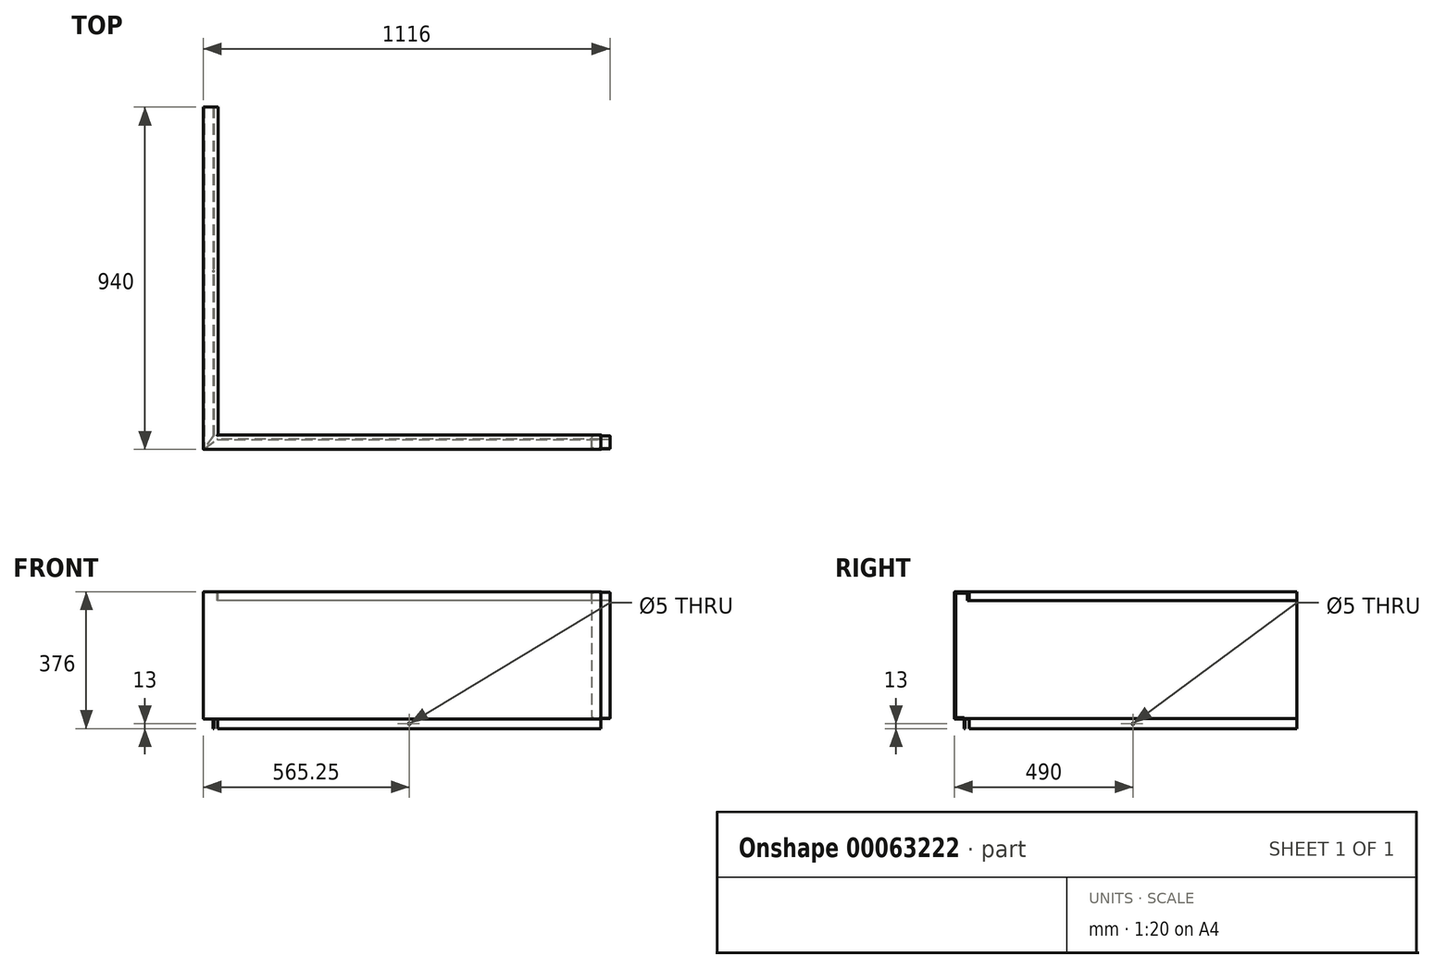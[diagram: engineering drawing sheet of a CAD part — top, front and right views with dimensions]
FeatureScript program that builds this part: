
annotation { "Feature Type Name" : "Feature", "Feature Type Description" : "" }
export const myFeature = defineFeature(function(context is Context, id is Id, definition is map)
    precondition{}
    {
        {
            var Q0;
            Q0=qCreatedBy(makeId("Right.planeOp"),FACE);
            var sketch = newSketch(context, id + "F0", { "sketchPlane" : qUnion([Q0])});
            skLineSegment(sketch, "E0.0", {"start": v(-40, -350) * mm, "end": v(-13, -350) * mm});
            skLineSegment(sketch, "E0.1", {"start": v(-40, 0) * mm, "end": v(-40, -350) * mm});
            skLineSegment(sketch, "E1", {"start": v(-38, -348) * mm, "end": v(-11, -348) * mm});
            skLineSegment(sketch, "E2", {"start": v(-38, -2) * mm, "end": v(-38, -348) * mm});
            skLineSegment(sketch, "E3", {"start": v(-2, -2) * mm, "end": v(-38, -2) * mm});
            skLineSegment(sketch, "E4", {"start": v(-2, -25) * mm, "end": v(-2, -2) * mm});
            skLineSegment(sketch, "E5", {"start": v(-13, -350) * mm, "end": v(-13, -376) * mm});
            skLineSegment(sketch, "E6", {"start": v(-11, -348) * mm, "end": v(-11, -376) * mm});
            skLineSegment(sketch, "E0.2", {"start": v(0, 0) * mm, "end": v(-40, 0) * mm});
            skLineSegment(sketch, "E0.3", {"start": v(0, -25) * mm, "end": v(0, 0) * mm});
            skLineSegment(sketch, "E7", {"start": v(0, -25) * mm, "end": v(-2, -25) * mm});
            skLineSegment(sketch, "E8", {"start": v(-11, -376) * mm, "end": v(-13, -376) * mm});
            skSolve(sketch);
        }
        {
            var Q0;
            Q0=makeQuery(id+"F0.imprint","IMPRINT",FACE,{"disambiguationData":[TD([[makeQuery(id+"F0.imprint","IMPRINT",EDGE,{"derivedFrom":sQuery(id+"F0.wireOp",EDGE,"E0.0")}),1.0]])]});
            extrude(context, id + "F1", {"entities" : qUnion([Q0]), "depth" : 1051 * mm, "hasSecondDirection" : true, "secondDirectionOppositeDirection" : true, "secondDirectionDepth" : .5 * mm});
        }
        {
            var Q0;
            Q0=qCreatedBy(makeId("Front.planeOp"),FACE);
            var sketch = newSketch(context, id + "F2", { "sketchPlane" : qUnion([Q0])});
            skLineSegment(sketch, "E9.0", {"start": v(-40, -350) * mm, "end": v(-13, -350) * mm});
            skLineSegment(sketch, "E9.1", {"start": v(-40, 0) * mm, "end": v(-40, -350) * mm});
            skLineSegment(sketch, "E10", {"start": v(-38, -348) * mm, "end": v(-11, -348) * mm});
            skLineSegment(sketch, "E11", {"start": v(-38, -2) * mm, "end": v(-38, -348) * mm});
            skLineSegment(sketch, "E12", {"start": v(-2, -2) * mm, "end": v(-38, -2) * mm});
            skLineSegment(sketch, "E13", {"start": v(-2, -25) * mm, "end": v(-2, -2) * mm});
            skLineSegment(sketch, "E14", {"start": v(-13, -350) * mm, "end": v(-13, -376) * mm});
            skLineSegment(sketch, "E15", {"start": v(-11, -348) * mm, "end": v(-11, -376) * mm});
            skLineSegment(sketch, "E9.2", {"start": v(0, 0) * mm, "end": v(-40, 0) * mm});
            skLineSegment(sketch, "E9.3", {"start": v(0, -25) * mm, "end": v(0, 0) * mm});
            skLineSegment(sketch, "E16", {"start": v(0, -25) * mm, "end": v(-2, -25) * mm});
            skLineSegment(sketch, "E17", {"start": v(-11, -376) * mm, "end": v(-13, -376) * mm});
            skSolve(sketch);
        }
        {
            var Q0;
            Q0=qSketchRegion(id+"F2",true);
            extrude(context, id + "F3", {"entities" : qUnion([Q0]), "oppositeDirection" : true, "depth" : 900 * mm});
        }
        {
            var Q0;
            Q0=qCreatedBy(makeId("Top.planeOp"),FACE);
            var sketch = newSketch(context, id + "F4", { "sketchPlane" : qUnion([Q0])});
            skLineSegment(sketch, "E18.top", {"start": v(0, 0) * mm, "end": v(-40, 0) * mm});
            skLineSegment(sketch, "E19.top", {"start": v(0, -40) * mm, "end": v(-40, -40) * mm});
            skLineSegment(sketch, "E19.left", {"start": v(0, 0) * mm, "end": v(0, -40) * mm});
            skLineSegment(sketch, "E19.right", {"start": v(-40, 0) * mm, "end": v(-40, -40) * mm});
            skSolve(sketch);
        }
        {
            var Q0;
            Q0=qSketchRegion(id+"F4",true);
            extrude(context, id + "F5", {"entities" : qUnion([Q0]), "oppositeDirection" : true, "depth" : 2 * mm});
        }
        {
            var Q0;
            Q0=makeQuery(id+"F5.opExtrude","CAP_FACE",FACE,{"disambiguationData":[OSD([sQuery(id+"F4.wireOp",EDGE,"E18.top"),sQuery(id+"F4.wireOp",EDGE,"E19.top"),sQuery(id+"F4.wireOp",EDGE,"E19.left"),sQuery(id+"F4.wireOp",EDGE,"E19.right")])],"isStart":false});
            var sketch = newSketch(context, id + "F6", { "sketchPlane" : qUnion([Q0])});
            skLineSegment(sketch, "E20.0", {"start": v(-40, 0) * mm, "end": v(-40, 40) * mm});
            skLineSegment(sketch, "E21.0", {"start": v(0, 40) * mm, "end": v(-40, 40) * mm});
            skLineSegment(sketch, "E22.0", {"start": v(0, 38) * mm, "end": v(-38, 38) * mm});
            skLineSegment(sketch, "E22.1", {"start": v(-38, 0) * mm, "end": v(-38, 38) * mm});
            skLineSegment(sketch, "E23", {"start": v(-38, 0) * mm, "end": v(-40, 0) * mm});
            skLineSegment(sketch, "E24", {"start": v(0, 40) * mm, "end": v(0, 38) * mm});
            skSolve(sketch);
        }
        {
            var Q0;
            Q0=makeQuery(id+"F6.imprint","IMPRINT",FACE,{"disambiguationData":[TD([[makeQuery(id+"F6.imprint","IMPRINT",EDGE,{"derivedFrom":sQuery(id+"F6.wireOp",EDGE,"E20.0")}),-1.0]])]});
            extrude(context, id + "F7", {"entities" : qUnion([Q0]), "depth" : 346 * mm});
        }
        {
            var Q0;
            Q0=makeQuery(id+"F7.opExtrude","CAP_FACE",FACE,{"disambiguationData":[OSD([sQuery(id+"F6.wireOp",EDGE,"E20.0"),sQuery(id+"F6.wireOp",EDGE,"E21.0"),sQuery(id+"F6.wireOp",EDGE,"E22.0"),sQuery(id+"F6.wireOp",EDGE,"E22.1"),sQuery(id+"F6.wireOp",EDGE,"E23"),sQuery(id+"F6.wireOp",EDGE,"E24")])],"isStart":false});
            var sketch = newSketch(context, id + "F8", { "sketchPlane" : qUnion([Q0])});
            skLineSegment(sketch, "E25.0", {"start": v(-40, 0) * mm, "end": v(-40, 40) * mm});
            skLineSegment(sketch, "E26.0", {"start": v(0, 40) * mm, "end": v(-40, 40) * mm});
            skLineSegment(sketch, "E27", {"start": v(-40, 0) * mm, "end": v(-11, 0) * mm});
            skLineSegment(sketch, "E28", {"start": v(-11, 0) * mm, "end": v(-38, 38) * mm});
            skLineSegment(sketch, "E29", {"start": v(-38, 38) * mm, "end": v(-0.5, 11) * mm});
            skLineSegment(sketch, "E30", {"start": v(-0.5, 11) * mm, "end": v(0, 40) * mm});
            skSolve(sketch);
        }
        {
            var Q0;
            Q0=qSketchRegion(id+"F8",true);
            extrude(context, id + "F9", {"entities" : qUnion([Q0]), "depth" : 2 * mm});
        }
        {
            var Q0;
            Q0=makeQuery(id+"F3.opExtrude","SWEPT_BODY",BODY,{"disambiguationData":[OSD([sQuery(id+"F2.wireOp",EDGE,"E9.0"),sQuery(id+"F2.wireOp",EDGE,"E9.1"),sQuery(id+"F2.wireOp",EDGE,"E10"),sQuery(id+"F2.wireOp",EDGE,"E11"),sQuery(id+"F2.wireOp",EDGE,"E12"),sQuery(id+"F2.wireOp",EDGE,"E13"),sQuery(id+"F2.wireOp",EDGE,"E14"),sQuery(id+"F2.wireOp",EDGE,"E15"),sQuery(id+"F2.wireOp",EDGE,"E9.2"),sQuery(id+"F2.wireOp",EDGE,"E9.3"),sQuery(id+"F2.wireOp",EDGE,"E16"),sQuery(id+"F2.wireOp",EDGE,"E17")])]});
            var Q1;
            Q1=makeQuery(id+"F7.opExtrude","SWEPT_BODY",BODY,{"disambiguationData":[OSD([sQuery(id+"F6.wireOp",EDGE,"E20.0"),sQuery(id+"F6.wireOp",EDGE,"E21.0"),sQuery(id+"F6.wireOp",EDGE,"E22.0"),sQuery(id+"F6.wireOp",EDGE,"E22.1"),sQuery(id+"F6.wireOp",EDGE,"E23"),sQuery(id+"F6.wireOp",EDGE,"E24")])]});
            var Q2;
            Q2=makeQuery(id+"F9.opExtrude","SWEPT_BODY",BODY,{"disambiguationData":[OSD([sQuery(id+"F8.wireOp",EDGE,"E25.0"),sQuery(id+"F8.wireOp",EDGE,"E26.0"),sQuery(id+"F8.wireOp",EDGE,"E27"),sQuery(id+"F8.wireOp",EDGE,"E28"),sQuery(id+"F8.wireOp",EDGE,"E29"),sQuery(id+"F8.wireOp",EDGE,"E30")])]});
            var Q3;
            Q3=makeQuery(id+"F5.opExtrude","SWEPT_BODY",BODY,{"disambiguationData":[OSD([sQuery(id+"F4.wireOp",EDGE,"E18.top"),sQuery(id+"F4.wireOp",EDGE,"E19.top"),sQuery(id+"F4.wireOp",EDGE,"E19.left"),sQuery(id+"F4.wireOp",EDGE,"E19.right")])]});
            booleanBodies(context, id + "F10", {"operationType" : BooleanOperationType.UNION, "tools" : qUnion([Q0, Q1, Q2, Q3])});
        }
        {
            var Q0;
            Q0=makeQuery(id+"F3.opExtrude","SWEPT_BODY",BODY,{"disambiguationData":[OSD([sQuery(id+"F2.wireOp",EDGE,"E9.0"),sQuery(id+"F2.wireOp",EDGE,"E9.1"),sQuery(id+"F2.wireOp",EDGE,"E10"),sQuery(id+"F2.wireOp",EDGE,"E11"),sQuery(id+"F2.wireOp",EDGE,"E12"),sQuery(id+"F2.wireOp",EDGE,"E13"),sQuery(id+"F2.wireOp",EDGE,"E14"),sQuery(id+"F2.wireOp",EDGE,"E15"),sQuery(id+"F2.wireOp",EDGE,"E9.2"),sQuery(id+"F2.wireOp",EDGE,"E9.3"),sQuery(id+"F2.wireOp",EDGE,"E16"),sQuery(id+"F2.wireOp",EDGE,"E17")])]});
            var Q1;
            Q1=makeQuery(id+"F1.opExtrude","SWEPT_BODY",BODY,{"disambiguationData":[OSD([sQuery(id+"F0.wireOp",EDGE,"E0.0"),sQuery(id+"F0.wireOp",EDGE,"E0.1"),sQuery(id+"F0.wireOp",EDGE,"E1"),sQuery(id+"F0.wireOp",EDGE,"E2"),sQuery(id+"F0.wireOp",EDGE,"E3"),sQuery(id+"F0.wireOp",EDGE,"E4"),sQuery(id+"F0.wireOp",EDGE,"E5"),sQuery(id+"F0.wireOp",EDGE,"E6"),sQuery(id+"F0.wireOp",EDGE,"E0.2"),sQuery(id+"F0.wireOp",EDGE,"E0.3"),sQuery(id+"F0.wireOp",EDGE,"E7"),sQuery(id+"F0.wireOp",EDGE,"E8")])]});
            booleanBodies(context, id + "F11", {"operationType" : BooleanOperationType.UNION, "tools" : qUnion([Q0, Q1])});
        }
        {
            var Q0;
            Q0=makeQuery(id+"F1.opExtrude","SWEPT_FACE",FACE,{"disambiguationData":[OSD([sQuery(id+"F0.wireOp",EDGE,"E5")])]});
            var sketch = newSketch(context, id + "F12", { "sketchPlane" : qUnion([Q0])});
            skLineSegment(sketch, "E31", {"start": v(-0.5, -363) * mm, "end": v(1051, -363) * mm});
            skPoint(sketch, "E32", {"position": v(525.25, -363) * mm});
            skSolve(sketch);
        }
        {
            var Q0;
            Q0=makeQuery(id+"F3.opExtrude","SWEPT_FACE",FACE,{"disambiguationData":[OSD([sQuery(id+"F2.wireOp",EDGE,"E14")])]});
            var sketch = newSketch(context, id + "F13", { "sketchPlane" : qUnion([Q0])});
            skLineSegment(sketch, "E33", {"start": v(-900, -363) * mm, "end": v(0, -363) * mm});
            skPoint(sketch, "E34", {"position": v(-450, -363) * mm});
            skSolve(sketch);
        }
        {
            var Q0;
            Q0=sQuery(id+"F13.wireOp",VERTEX,"E34");
            var Q1;
            Q1=sQuery(id+"F12.wireOp",VERTEX,"E32");
            var Q2;
            Q2=makeQuery(id+"F3.opExtrude","SWEPT_BODY",BODY,{"disambiguationData":[OSD([sQuery(id+"F2.wireOp",EDGE,"E9.0"),sQuery(id+"F2.wireOp",EDGE,"E9.1"),sQuery(id+"F2.wireOp",EDGE,"E10"),sQuery(id+"F2.wireOp",EDGE,"E11"),sQuery(id+"F2.wireOp",EDGE,"E12"),sQuery(id+"F2.wireOp",EDGE,"E13"),sQuery(id+"F2.wireOp",EDGE,"E14"),sQuery(id+"F2.wireOp",EDGE,"E15"),sQuery(id+"F2.wireOp",EDGE,"E9.2"),sQuery(id+"F2.wireOp",EDGE,"E9.3"),sQuery(id+"F2.wireOp",EDGE,"E16"),sQuery(id+"F2.wireOp",EDGE,"E17")])]});
            hole(context, id + "F14", {"style" : HoleStyle.SIMPLE, "holeDiameter" : 5 * mm, "endStyle" : HoleEndStyle.THROUGH, "locations" : qUnion([Q0, Q1]), "scope" : qUnion([Q2])});
        }
        {
            var Q0;
            Q0=makeQuery(id+"F1.opExtrude","CAP_FACE",FACE,{"disambiguationData":[OSD([sQuery(id+"F0.wireOp",EDGE,"E0.0"),sQuery(id+"F0.wireOp",EDGE,"E0.1"),sQuery(id+"F0.wireOp",EDGE,"E1"),sQuery(id+"F0.wireOp",EDGE,"E2"),sQuery(id+"F0.wireOp",EDGE,"E3"),sQuery(id+"F0.wireOp",EDGE,"E4"),sQuery(id+"F0.wireOp",EDGE,"E5"),sQuery(id+"F0.wireOp",EDGE,"E6"),sQuery(id+"F0.wireOp",EDGE,"E0.2"),sQuery(id+"F0.wireOp",EDGE,"E0.3"),sQuery(id+"F0.wireOp",EDGE,"E7"),sQuery(id+"F0.wireOp",EDGE,"E8")])],"isStart":false});
            var sketch = newSketch(context, id + "F15", { "sketchPlane" : qUnion([Q0])});
            skLineSegment(sketch, "E35.0", {"start": v(-36, -346) * mm, "end": v(-13, -346) * mm});
            skLineSegment(sketch, "E35.1", {"start": v(-36, -4) * mm, "end": v(-36, -346) * mm});
            skLineSegment(sketch, "E35.2", {"start": v(-4, -4) * mm, "end": v(-36, -4) * mm});
            skLineSegment(sketch, "E35.3", {"start": v(-4, -25) * mm, "end": v(-4, -4) * mm});
            skLineSegment(sketch, "E36.0", {"start": v(-2, -25) * mm, "end": v(-2, -2) * mm});
            skLineSegment(sketch, "E37.0", {"start": v(-2, -2) * mm, "end": v(-38, -2) * mm});
            skLineSegment(sketch, "E38.0", {"start": v(-38, -2) * mm, "end": v(-38, -348) * mm});
            skLineSegment(sketch, "E39.0", {"start": v(-38, -348) * mm, "end": v(-13, -348) * mm});
            skLineSegment(sketch, "E40", {"start": v(-13, -346) * mm, "end": v(-13, -348) * mm});
            skLineSegment(sketch, "E41", {"start": v(-4, -25) * mm, "end": v(-2, -25) * mm});
            skSolve(sketch);
        }
        {
            var Q0;
            Q0=qSketchRegion(id+"F15",true);
            extrude(context, id + "F16", {"entities" : qUnion([Q0]), "operationType" : NewBodyOperationType.ADD, "depth" : 25 * mm, "hasSecondDirection" : true, "secondDirectionOppositeDirection" : true, "secondDirectionDepth" : 25 * mm});
        }
        {
            var Q0;
            Q0=makeQuery(id+"F1.opExtrude","SWEPT_EDGE",EDGE,{"disambiguationData":[OSD([sQuery(id+"F0.wireOp",EDGE,"E0.2"),sQuery(id+"F0.wireOp",EDGE,"E0.3")])]});
            var Q1;
            Q1=makeQuery(id+"F16.opExtrude","SWEPT_EDGE",EDGE,{"disambiguationData":[OSD([sQuery(id+"F15.wireOp",EDGE,"E36.0"),sQuery(id+"F15.wireOp",EDGE,"E37.0")])]});
            var Q2;
            Q2=makeQuery(id+"F11.opBoolean","MERGE",EDGE,{"derivedFrom":[makeQuery(id+"F1.opExtrude","SWEPT_EDGE",EDGE,{"disambiguationData":[OSD([sQuery(id+"F0.wireOp",EDGE,"E0.1"),sQuery(id+"F0.wireOp",EDGE,"E0.2")])]}),makeQuery(id+"F5.opExtrude","CAP_EDGE",EDGE,{"disambiguationData":[OSD([sQuery(id+"F4.wireOp",EDGE,"E19.top")])],"isStart":true})]});
            var Q3;
            Q3=makeQuery(id+"F16.opExtrude","SWEPT_EDGE",EDGE,{"disambiguationData":[OSD([sQuery(id+"F15.wireOp",EDGE,"E37.0"),sQuery(id+"F15.wireOp",EDGE,"E38.0")])]});
            var Q4;
            Q4=makeQuery(id+"F10.opBoolean","MERGE",EDGE,{"derivedFrom":[makeQuery(id+"F3.opExtrude","SWEPT_EDGE",EDGE,{"disambiguationData":[OSD([sQuery(id+"F2.wireOp",EDGE,"E9.1"),sQuery(id+"F2.wireOp",EDGE,"E9.2")])]}),makeQuery(id+"F5.opExtrude","CAP_EDGE",EDGE,{"disambiguationData":[OSD([sQuery(id+"F4.wireOp",EDGE,"E19.right")])],"isStart":true})]});
            var Q5;
            Q5=makeQuery(id+"F10.opBoolean","MERGE",EDGE,{"derivedFrom":[makeQuery(id+"F3.opExtrude","SWEPT_EDGE",EDGE,{"disambiguationData":[OSD([sQuery(id+"F2.wireOp",EDGE,"E9.2"),sQuery(id+"F2.wireOp",EDGE,"E9.3")])]}),makeQuery(id+"F5.opExtrude","CAP_EDGE",EDGE,{"disambiguationData":[OSD([sQuery(id+"F4.wireOp",EDGE,"E19.left")])],"isStart":true})]});
            var Q6;
            Q6=makeQuery(id+"F3.opExtrude","SWEPT_EDGE",EDGE,{"disambiguationData":[OSD([sQuery(id+"F2.wireOp",EDGE,"E10"),sQuery(id+"F2.wireOp",EDGE,"E15")])]});
            var Q7;
            Q7=makeQuery(id+"F10.opBoolean","MERGE",EDGE,{"derivedFrom":[makeQuery(id+"F3.opExtrude","SWEPT_EDGE",EDGE,{"disambiguationData":[OSD([sQuery(id+"F2.wireOp",EDGE,"E10"),sQuery(id+"F2.wireOp",EDGE,"E11")])]}),makeQuery(id+"F7.opExtrude","CAP_EDGE",EDGE,{"disambiguationData":[OSD([sQuery(id+"F6.wireOp",EDGE,"E22.1")])],"isStart":false})]});
            var Q8;
            {var subQ0=sQuery(id+"F6.wireOp",EDGE,"E22.0");var subQ10=makeQuery(id+"F7.opExtrude","CAP_EDGE",EDGE,{"disambiguationData":[OSD([subQ0])],"isStart":false});Q8=makeQuery(id+"F11.opBoolean","MERGE",EDGE,{"derivedFrom":[makeQuery(id+"F1.opExtrude","SWEPT_EDGE",EDGE,{"disambiguationData":[OSD([sQuery(id+"F0.wireOp",EDGE,"E1"),sQuery(id+"F0.wireOp",EDGE,"E2")])]}),makeQuery(id+"F10.opBoolean","SPLIT",EDGE,{"disambiguationData":[TD([makeQuery(id+"F3.opExtrude","SWEPT_FACE",FACE,{"disambiguationData":[OSD([sQuery(id+"F2.wireOp",EDGE,"E9.3")])]})])],"derivedFrom":subQ10}),makeQuery(id+"F10.opBoolean","SPLIT",EDGE,{"disambiguationData":[TD([makeQuery(id+"F3.opExtrude","SWEPT_FACE",FACE,{"disambiguationData":[OSD([sQuery(id+"F2.wireOp",EDGE,"E10")])]})])],"derivedFrom":subQ10})]});}
            var Q9;
            Q9=makeQuery(id+"F1.opExtrude","SWEPT_EDGE",EDGE,{"disambiguationData":[OSD([sQuery(id+"F0.wireOp",EDGE,"E1"),sQuery(id+"F0.wireOp",EDGE,"E6")])]});
            var Q10;
            Q10=makeQuery(id+"F16.opExtrude","SWEPT_EDGE",EDGE,{"disambiguationData":[OSD([sQuery(id+"F15.wireOp",EDGE,"E35.0"),sQuery(id+"F15.wireOp",EDGE,"E35.1")])]});
            var Q11;
            Q11=makeQuery(id+"F1.opExtrude","SWEPT_EDGE",EDGE,{"disambiguationData":[OSD([sQuery(id+"F0.wireOp",EDGE,"E0.0"),sQuery(id+"F0.wireOp",EDGE,"E5")])]});
            var Q12;
            Q12=makeQuery(id+"F11.opBoolean","MERGE",EDGE,{"derivedFrom":[makeQuery(id+"F1.opExtrude","SWEPT_EDGE",EDGE,{"disambiguationData":[OSD([sQuery(id+"F0.wireOp",EDGE,"E0.0"),sQuery(id+"F0.wireOp",EDGE,"E0.1")])]}),makeQuery(id+"F9.opExtrude","CAP_EDGE",EDGE,{"disambiguationData":[OSD([sQuery(id+"F8.wireOp",EDGE,"E26.0")])],"isStart":false})]});
            var Q13;
            Q13=makeQuery(id+"F16.opExtrude","SWEPT_EDGE",EDGE,{"disambiguationData":[OSD([sQuery(id+"F15.wireOp",EDGE,"E38.0"),sQuery(id+"F15.wireOp",EDGE,"E39.0")])]});
            var Q14;
            Q14=makeQuery(id+"F3.opExtrude","SWEPT_EDGE",EDGE,{"disambiguationData":[OSD([sQuery(id+"F2.wireOp",EDGE,"E9.0"),sQuery(id+"F2.wireOp",EDGE,"E14")])]});
            var Q15;
            Q15=makeQuery(id+"F10.opBoolean","MERGE",EDGE,{"derivedFrom":[makeQuery(id+"F3.opExtrude","SWEPT_EDGE",EDGE,{"disambiguationData":[OSD([sQuery(id+"F2.wireOp",EDGE,"E9.0"),sQuery(id+"F2.wireOp",EDGE,"E9.1")])]}),makeQuery(id+"F9.opExtrude","CAP_EDGE",EDGE,{"disambiguationData":[OSD([sQuery(id+"F8.wireOp",EDGE,"E25.0")])],"isStart":false})]});
            var Q16;
            Q16=makeQuery(id+"F11.opBoolean","MERGE",EDGE,{"derivedFrom":[makeQuery(id+"F1.opExtrude","SWEPT_EDGE",EDGE,{"disambiguationData":[OSD([sQuery(id+"F0.wireOp",EDGE,"E2"),sQuery(id+"F0.wireOp",EDGE,"E3")])]}),makeQuery(id+"F7.opExtrude","CAP_EDGE",EDGE,{"disambiguationData":[OSD([sQuery(id+"F6.wireOp",EDGE,"E22.0")])],"isStart":true})]});
            var Q17;
            Q17=makeQuery(id+"F10.opBoolean","MERGE",EDGE,{"derivedFrom":[makeQuery(id+"F3.opExtrude","SWEPT_EDGE",EDGE,{"disambiguationData":[OSD([sQuery(id+"F2.wireOp",EDGE,"E11"),sQuery(id+"F2.wireOp",EDGE,"E12")])]}),makeQuery(id+"F7.opExtrude","CAP_EDGE",EDGE,{"disambiguationData":[OSD([sQuery(id+"F6.wireOp",EDGE,"E22.1")])],"isStart":true})]});
            var Q18;
            Q18=makeQuery(id+"F3.opExtrude","SWEPT_EDGE",EDGE,{"disambiguationData":[OSD([sQuery(id+"F2.wireOp",EDGE,"E12"),sQuery(id+"F2.wireOp",EDGE,"E13")])]});
            var Q19;
            Q19=makeQuery(id+"F16.opExtrude","SWEPT_EDGE",EDGE,{"disambiguationData":[OSD([sQuery(id+"F15.wireOp",EDGE,"E35.2"),sQuery(id+"F15.wireOp",EDGE,"E35.3")])]});
            var Q20;
            Q20=makeQuery(id+"F1.opExtrude","SWEPT_EDGE",EDGE,{"disambiguationData":[OSD([sQuery(id+"F0.wireOp",EDGE,"E3"),sQuery(id+"F0.wireOp",EDGE,"E4")])]});
            fillet(context, id + "F17", {"entities" : qUnion([Q0, Q1, Q2, Q3, Q4, Q5, Q6, Q7, Q8, Q9, Q10, Q11, Q12, Q13, Q14, Q15, Q16, Q17, Q18, Q19, Q20]), "radius" : 2 * mm, "tangentPropagation" : true, "allowEdgeOverflow" : false});
        }
    });
